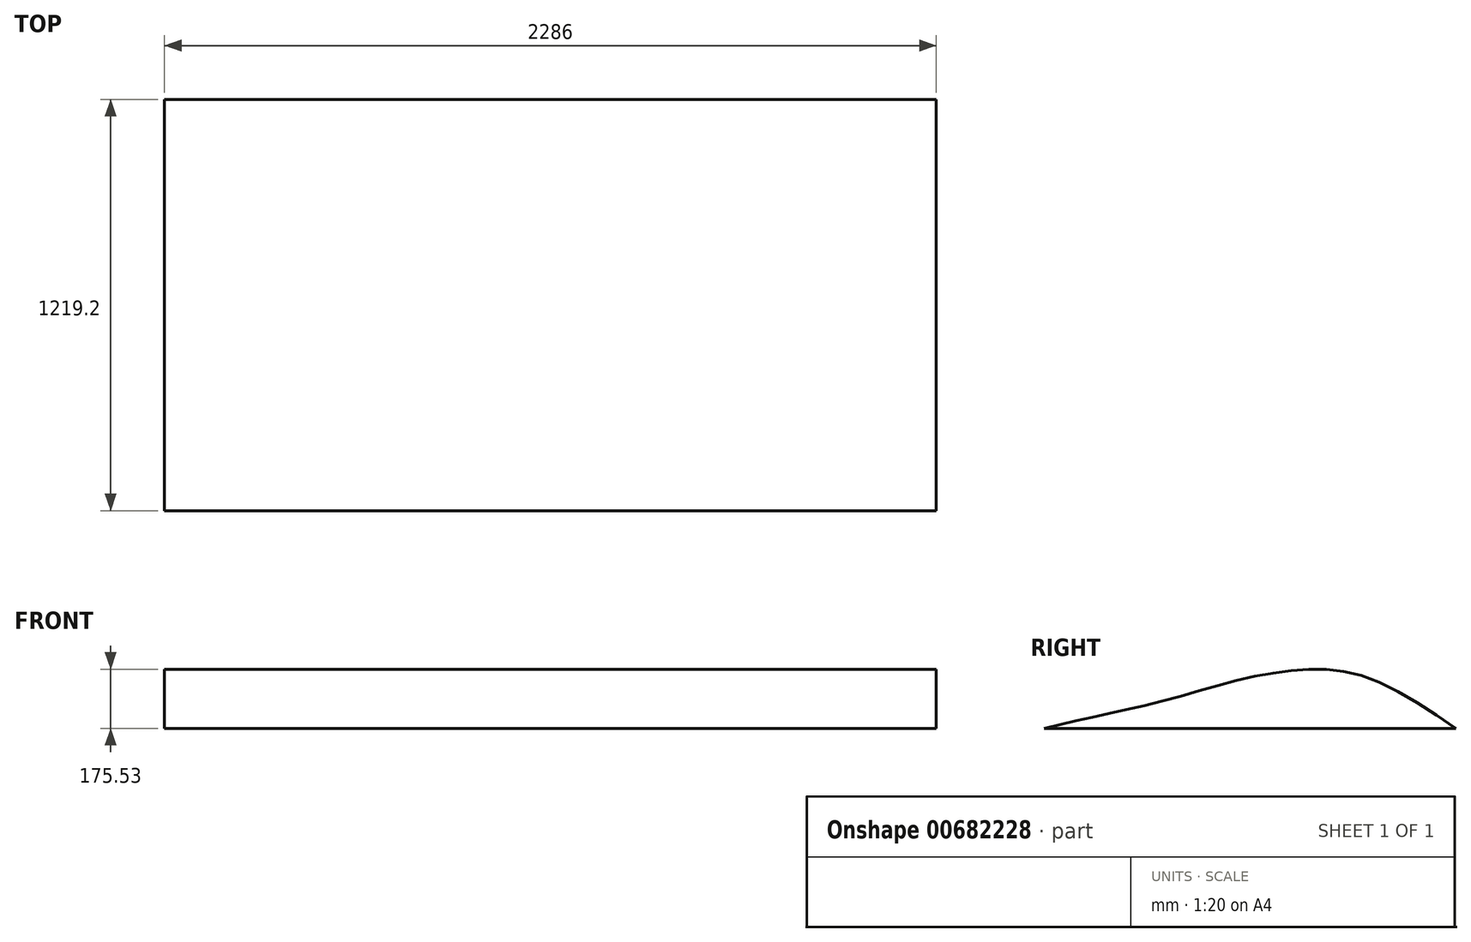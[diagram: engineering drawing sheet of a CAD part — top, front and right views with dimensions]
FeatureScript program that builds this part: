
annotation { "Feature Type Name" : "Feature", "Feature Type Description" : "" }
export const myFeature = defineFeature(function(context is Context, id is Id, definition is map)
    precondition{}
    {
        {
            var Q0;
            Q0=qCreatedBy(makeId("Right.planeOp"),FACE);
            var sketch = newSketch(context, id + "F0", { "sketchPlane" : qUnion([Q0])});
            skLineSegment(sketch, "E0", {"start": v(1219.2, 0) * mm, "end": v(0, 0) * mm});
            skFitSpline(sketch, "E1", {"points": [v(1219.2, 0) * mm, v(962.61, 149.23) * mm, v(774.7, 174.7) * mm, v(570.84, 142.86) * mm, v(354.25, 82.34) * mm, v(159.96, 37.75) * mm, v(0, 0) * mm], "startDerivative": vector(-1335.33, 907.74) * mm, "endDerivative": vector(-1064.63, -259.16) * mm});
            skSolve(sketch);
        }
        {
            var Q0;
            Q0 = qSketchRegion(id + "F0", true);
            extrude(context, id + "F1", {"entities" : qUnion([Q0]), "depth" : 2286 * mm, "offsetDistance" : 25.4 * mm});
        }
    });
